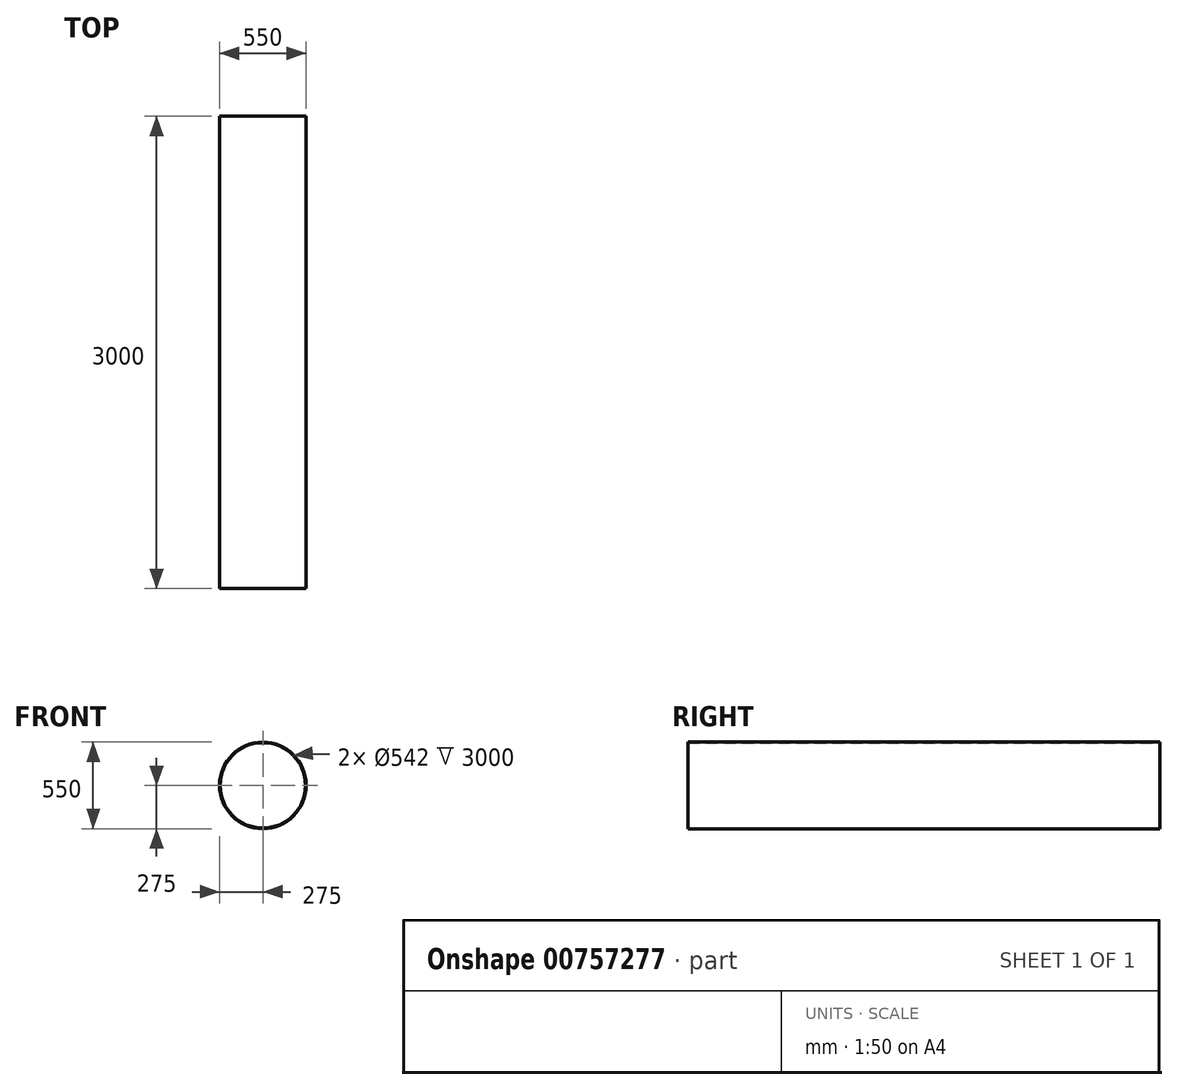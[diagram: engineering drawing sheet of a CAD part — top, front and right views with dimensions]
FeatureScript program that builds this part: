
annotation { "Feature Type Name" : "Feature", "Feature Type Description" : "" }
export const myFeature = defineFeature(function(context is Context, id is Id, definition is map)
    precondition{}
    {
        {
            var Q0;
            Q0=qCreatedBy(makeId("Front.planeOp"),FACE);
            var sketch = newSketch(context, id + "F0", { "sketchPlane" : qUnion([Q0])});
            skCircle(sketch, "E0", {"center": v(0, 0) * mm, "radius": 275 * mm});
            skCircle(sketch, "E1", {"center": v(0, 0) * mm, "radius": 271 * mm});
            skSolve(sketch);
        }
        {
            var Q0;
            Q0=makeQuery(id+"F0.imprint","IMPRINT",FACE,{"disambiguationData":[TD([[makeQuery(id+"F0.imprint","IMPRINT",EDGE,{"derivedFrom":sQuery(id+"F0.wireOp",EDGE,"E0")}),1.0]])]});
            extrude(context, id + "F1", {"entities" : qUnion([Q0]), "depth" : 3000 * mm, "offsetDistance" : 25 * mm});
        }
    });
